# Revit family: Faucet-Kitchen_Sink-KOHLER-Artifacts-K-99260
name_source: partatom
category: Plumbing Fixtures
revit_build: Autodesk Revit 2015 (Build: 20140606_1530(x64)
units: mm (PartAtom-declared; Revit-internal decimal feet)

## types (4) — shared parameters
ADA Compliant = Yes
CW Connection = Yes
Cold Water Inlet = Cold Water Inlet
Date Modified = 02/22/2018
Default Elevation = 36"
Description = Single-hole kitchen sink faucet with 17-5/8 inch pull-down spout, DockNetik magnetic docking system, and 3-function sprayhead featuring Sweep and BerrySoft spray
Faucet Hole Spacing = 0"
Flow Rate = 2 GPM
HW Connection = Yes
Height = 17 9/16"
Hot Water Inlet = Hot Water Inlet
Length = 11 13/32"
Manufacturer = KOHLER Co.
MasterFormat 1995 = 15410
MasterFormat 2004 = 22.41.39
Material = Premium Metal Construction
Pressure = 60.00 psi
Product Documentation Link = http://www.us.kohler.com
Product Name = Artifacts
Product Page URL = http://www.us.kohler.com
Spout Reach = 9 1/16"
URL = https://www.us.kohler.com
Vent Connection = No
Waste Connection = No
Waste Water Outlet = Waste Water Outlet
Width = 4 3/4"

## per-type parameters (varying)
| type | Assembly Code | Finish | Model | Type |
| CP- Polished Chrome | D2010 | Kohler-Metal-CP-Polished_Chrome | K-99260-CP | 1 |
| SN- Vibrant Polished Nickel | D2020 | Kohler-Metal-SN-Vibrant_Polished_Nickel | K-99260-SN | 2 |
| VS- Vibrant Stainless | D2020 | Kohler-Metal-VS-Vibrant_Stainless | K-99260-VS | 3 |
| 2BZ- Oil Rubbed Bronze | D2020 | Kohler-Metal-2BZ-Oil_Rubbed_Bronze | K-99260-2BZ | 4 |

## geometry (parser evidence)
native form markers: Sweep x17
no freeform markers — native parametric forms only
